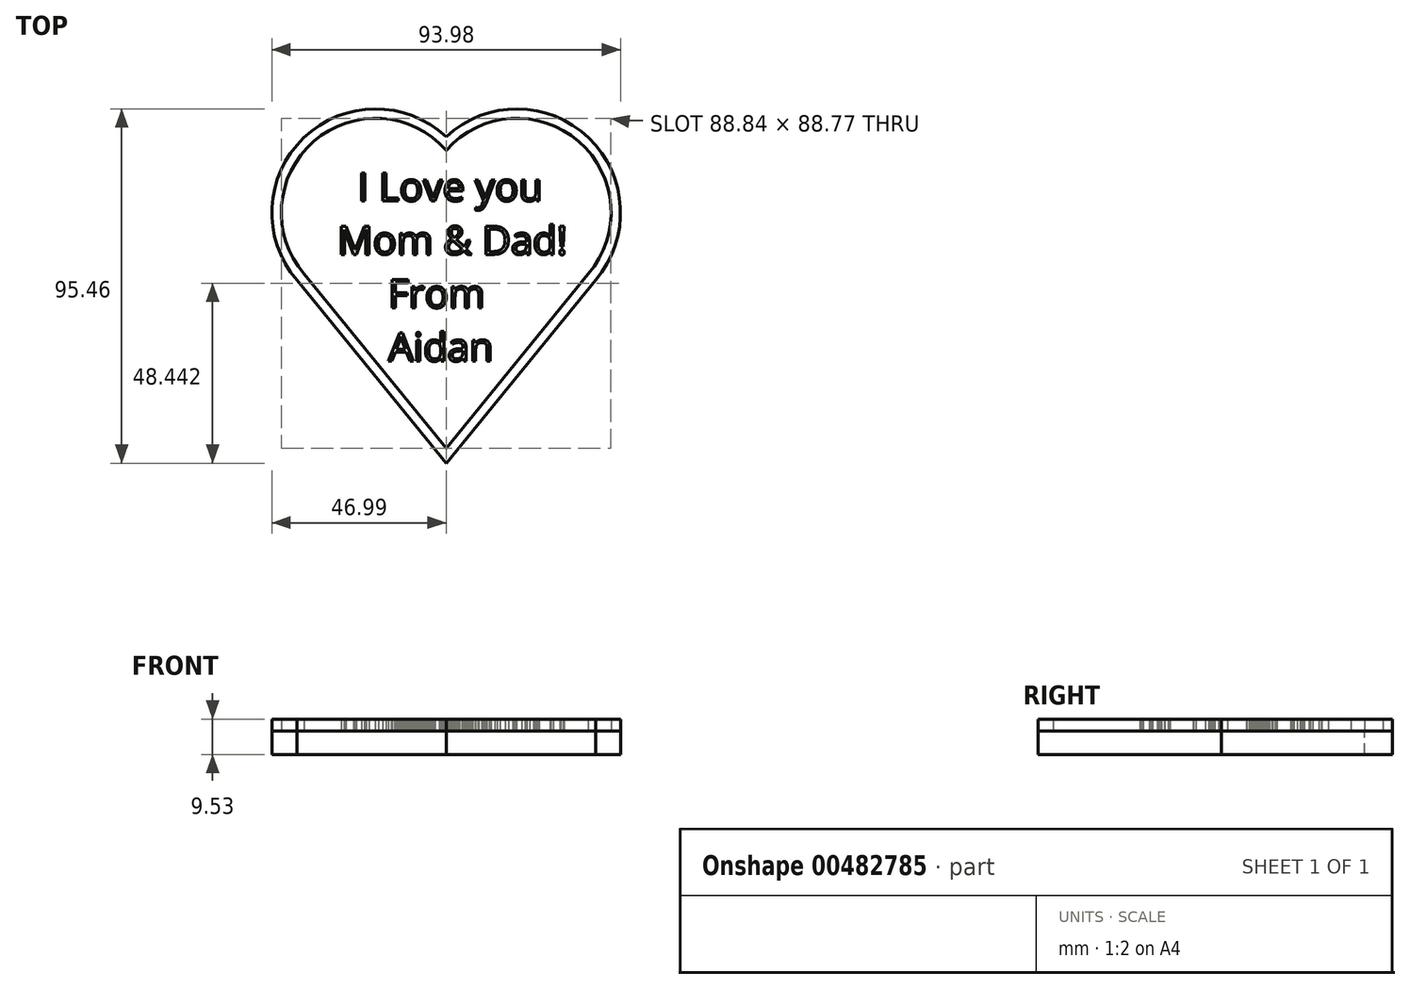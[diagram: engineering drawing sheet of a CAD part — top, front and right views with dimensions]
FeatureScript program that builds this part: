
annotation { "Feature Type Name" : "Feature", "Feature Type Description" : "" }
export const myFeature = defineFeature(function(context is Context, id is Id, definition is map)
    precondition{}
    {
        {
            var Q0;
            Q0=qCreatedBy(makeId("Top.planeOp"),FACE);
            var sketch = newSketch(context, id + "F0", { "sketchPlane" : qUnion([Q0])});
            skLineSegment(sketch, "E0", {"start": v(-19.05, 43.96) * mm, "end": v(-19.05, -49.28) * mm, "construction": true});
            skArc(sketch, "E1", {"start": v(0, 16.8) * mm, "mid": v(-35.73, 19.16) * mm, "end": v(-38.31, -16.56) * mm});
            skLineSegment(sketch, "E2", {"start": v(-38.31, -16.56) * mm, "end": v(0, -63.5) * mm});
            skArc(sketch, "E3.MirrorC", {"start": v(0, 16.8) * mm, "mid": v(35.73, 19.16) * mm, "end": v(38.31, -16.56) * mm});
            skLineSegment(sketch, "E4.MirrorCS", {"start": v(38.31, -16.56) * mm, "end": v(0, -63.5) * mm});
            skArc(sketch, "E5.0", {"start": v(0, 20.44) * mm, "mid": v(-38.4, 20.16) * mm, "end": v(-40.26, -18.19) * mm});
            skArc(sketch, "E5.1", {"start": v(0, 20.44) * mm, "mid": v(38.4, 20.16) * mm, "end": v(40.26, -18.19) * mm});
            skLineSegment(sketch, "E5.2", {"start": v(40.26, -18.19) * mm, "end": v(0, -67.52) * mm});
            skLineSegment(sketch, "E5.3", {"start": v(-40.26, -18.19) * mm, "end": v(0, -67.52) * mm});
            skSolve(sketch);
        }
        {
            var Q0;
            Q0=qCreatedBy(makeId("Top.planeOp"),FACE);
            var sketch = newSketch(context, id + "F1", { "sketchPlane" : qUnion([Q0])});
            skText(sketch, "E6", { "text": "  I Love you\nMom & Dad!\n     From\n     Aidan", "fontName": "OpenSans-Regular.ttf"});
            const initialGuessF1  = {"E6": [-0.02931, 0.00314, 1, 0, 0.00762]};
            skSetInitialGuess(sketch, initialGuessF1);
            skSolve(sketch);
        }
        {
            var Q0;
            Q0 = qSketchRegion(id + "F0", true);
            var Q1;
            Q1=makeQuery(id+"F0.imprint","IMPRINT",FACE,{"disambiguationData":[TD([[makeQuery(id+"F0.imprint","IMPRINT",EDGE,{"derivedFrom":sQuery(id+"F0.wireOp",EDGE,"E1")}),1.0]])]});
            extrude(context, id + "F2", {"entities" : qUnion([Q0, Q1]), "oppositeDirection" : true, "depth" : 6.35 * mm});
        }
        {
            var Q0;
            Q0 = qSketchRegion(id + "F0", true);
            extrude(context, id + "F3", {"entities" : qUnion([Q0]), "depth" : 3.17 * mm});
        }
        {
            var Q0;
            Q0 = qSketchRegion(id + "F1", true);
            extrude(context, id + "F4", {"entities" : qUnion([Q0]), "operationType" : NewBodyOperationType.ADD, "depth" : 3.17 * mm});
        }
    });
